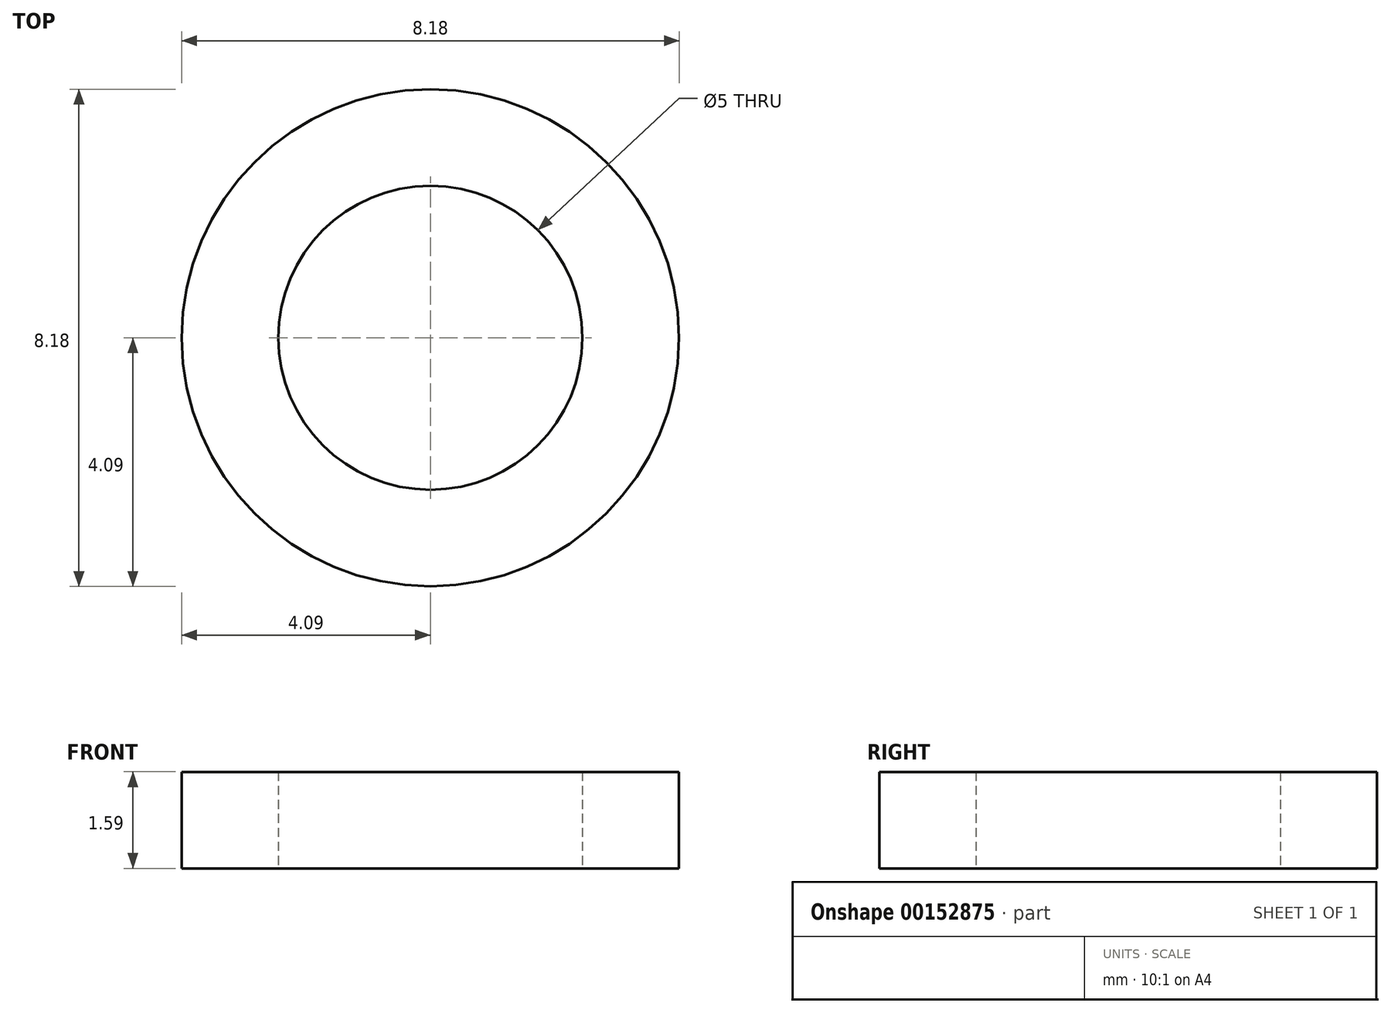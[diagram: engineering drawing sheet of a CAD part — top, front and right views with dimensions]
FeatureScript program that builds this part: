
annotation { "Feature Type Name" : "Feature", "Feature Type Description" : "" }
export const myFeature = defineFeature(function(context is Context, id is Id, definition is map)
    precondition{}
    {
        {
            var Q0;
            Q0=qCreatedBy(makeId("Top.planeOp"),FACE);
            var sketch = newSketch(context, id + "F0", { "sketchPlane" : qUnion([Q0])});
            skCircle(sketch, "E0", {"center": v(0, 0) * mm, "radius": 2.5 * mm});
            skCircle(sketch, "E1", {"center": v(0, 0) * mm, "radius": 4.09 * mm});
            skSolve(sketch);
        }
        {
            var Q0;
            Q0=qSketchRegion(id+"F0",true);
            extrude(context, id + "F1", {"entities" : qUnion([Q0]), "depth" : 1.59 * mm});
        }
    });
